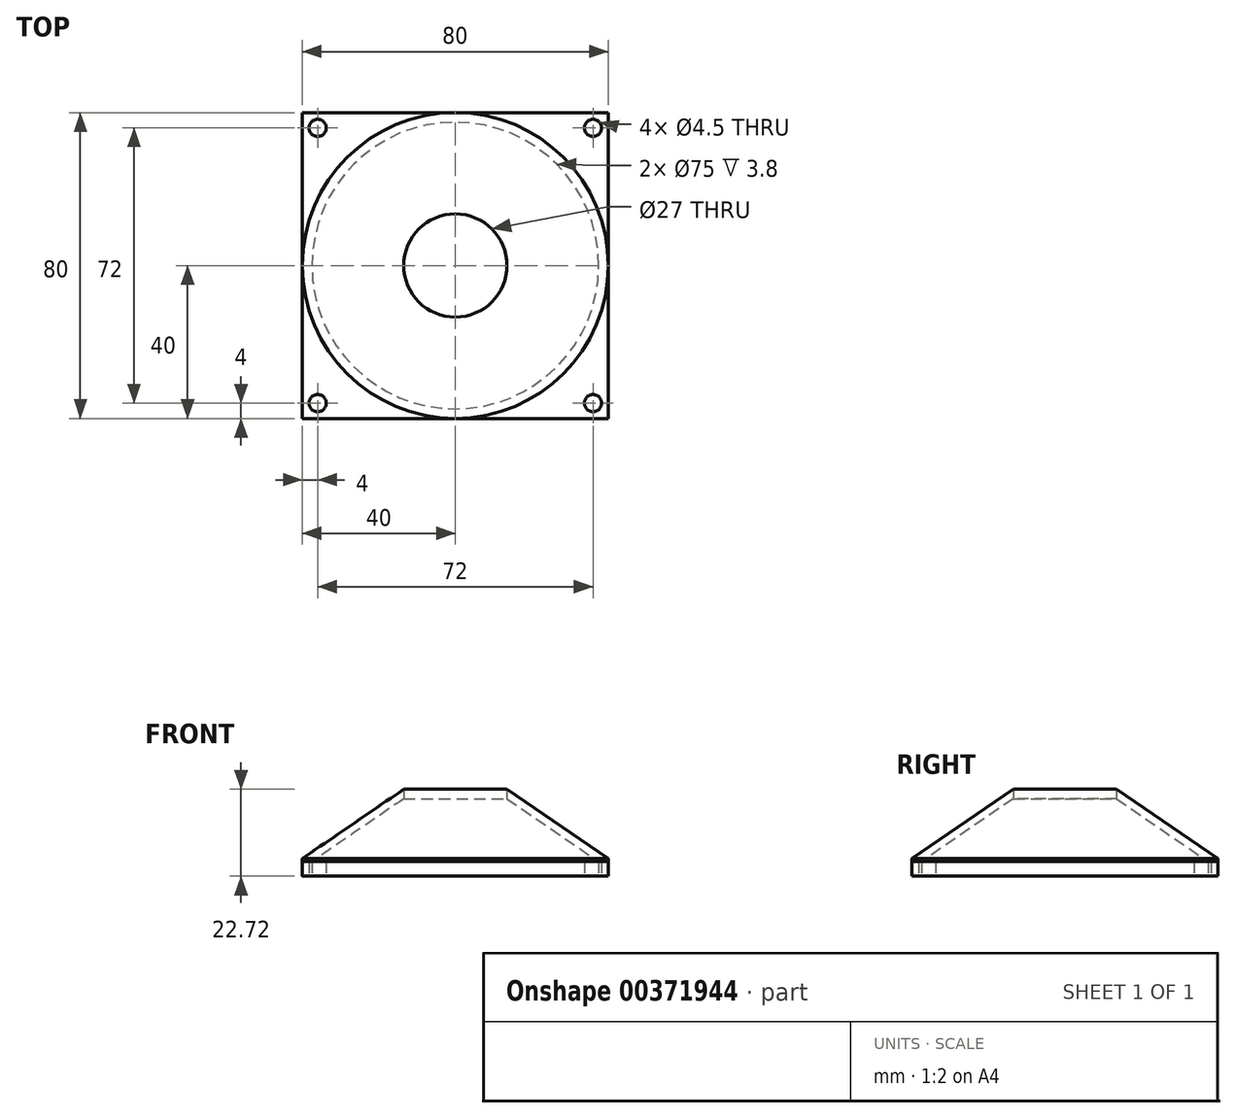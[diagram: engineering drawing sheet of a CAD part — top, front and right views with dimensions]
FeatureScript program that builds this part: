
annotation { "Feature Type Name" : "Feature", "Feature Type Description" : "" }
export const myFeature = defineFeature(function(context is Context, id is Id, definition is map)
    precondition{}
    {
        {
            var Q0;
            Q0=qCreatedBy(makeId("Top.planeOp"),FACE);
            var sketch = newSketch(context, id + "F0", { "sketchPlane" : qUnion([Q0])});
            skPoint(sketch, "E0.middle", {"position": v(0, 0) * mm});
            skCircle(sketch, "E1", {"center": v(0, 0) * mm, "radius": 37.5 * mm});
            skCircle(sketch, "E2", {"center": v(36, 36) * mm, "radius": 2.25 * mm});
            skPoint(sketch, "E3", {"position": v(37.62, 37.57) * mm});
            skCircle(sketch, "E4", {"center": v(36, -36) * mm, "radius": 2.25 * mm});
            skCircle(sketch, "E5", {"center": v(-36, -36) * mm, "radius": 2.25 * mm});
            skCircle(sketch, "E6", {"center": v(-36, 36) * mm, "radius": 2.25 * mm});
            skLineSegment(sketch, "E7.bottom", {"start": v(40, 40) * mm, "end": v(-40, 40) * mm});
            skLineSegment(sketch, "E7.top", {"start": v(40, -40) * mm, "end": v(-40, -40) * mm});
            skLineSegment(sketch, "E7.left", {"start": v(40, 40) * mm, "end": v(40, -40) * mm});
            skLineSegment(sketch, "E7.right", {"start": v(-40, 40) * mm, "end": v(-40, -40) * mm});
            skSolve(sketch);
        }
        {
            var Q0;
            Q0=makeQuery(id+"F0.imprint","IMPRINT",FACE,{"disambiguationData":[TD([[makeQuery(id+"F0.imprint","IMPRINT",EDGE,{"derivedFrom":sQuery(id+"F0.wireOp",EDGE,"E0.bottom")}),1.0]])]});
            var Q1;
            Q1=makeQuery(id+"F0.imprint","IMPRINT",FACE,{"disambiguationData":[TD([[makeQuery(id+"F0.imprint","IMPRINT",EDGE,{"derivedFrom":sQuery(id+"F0.wireOp",EDGE,"E1")}),-1.0]])]});
            extrude(context, id + "F1", {"entities" : qUnion([Q0, Q1]), "depth" : 3.8 * mm});
        }
        {
            var Q0;
            Q0=qCreatedBy(makeId("Right.planeOp"),FACE);
            var sketch = newSketch(context, id + "F2", { "sketchPlane" : qUnion([Q0])});
            skLineSegment(sketch, "E8", {"start": v(-37.5, 0) * mm, "end": v(-40, 0) * mm});
            skLineSegment(sketch, "E9", {"start": v(0, 0) * mm, "end": v(0, 55.75) * mm});
            skLineSegment(sketch, "E10", {"start": v(-40, 0) * mm, "end": v(-40, 3.8) * mm});
            skLineSegment(sketch, "E11", {"start": v(-37.5, 0) * mm, "end": v(-37.5, 3.8) * mm});
            skLineSegment(sketch, "E12", {"start": v(-13.5, 22.72) * mm, "end": v(-13.5, 20.22) * mm});
            skLineSegment(sketch, "E13", {"start": v(-13.5, 20.22) * mm, "end": v(-37.5, 3.8) * mm});
            skLineSegment(sketch, "E14", {"start": v(-13.5, 22.72) * mm, "end": v(-40, 4.59) * mm});
            skLineSegment(sketch, "E15", {"start": v(-40, 4.59) * mm, "end": v(-40, 3.8) * mm});
            skSolve(sketch);
        }
        {
            var Q0;
            Q0=qSketchRegion(id+"F2",true);
            var Q1;
            Q1=sQuery(id+"F2.wireOp",EDGE,"E9");
            revolve(context, id + "F3", {"entities" : qUnion([Q0]), "axis" : qUnion([Q1]), "revolveType" : RevolveType.FULL});
        }
    });
